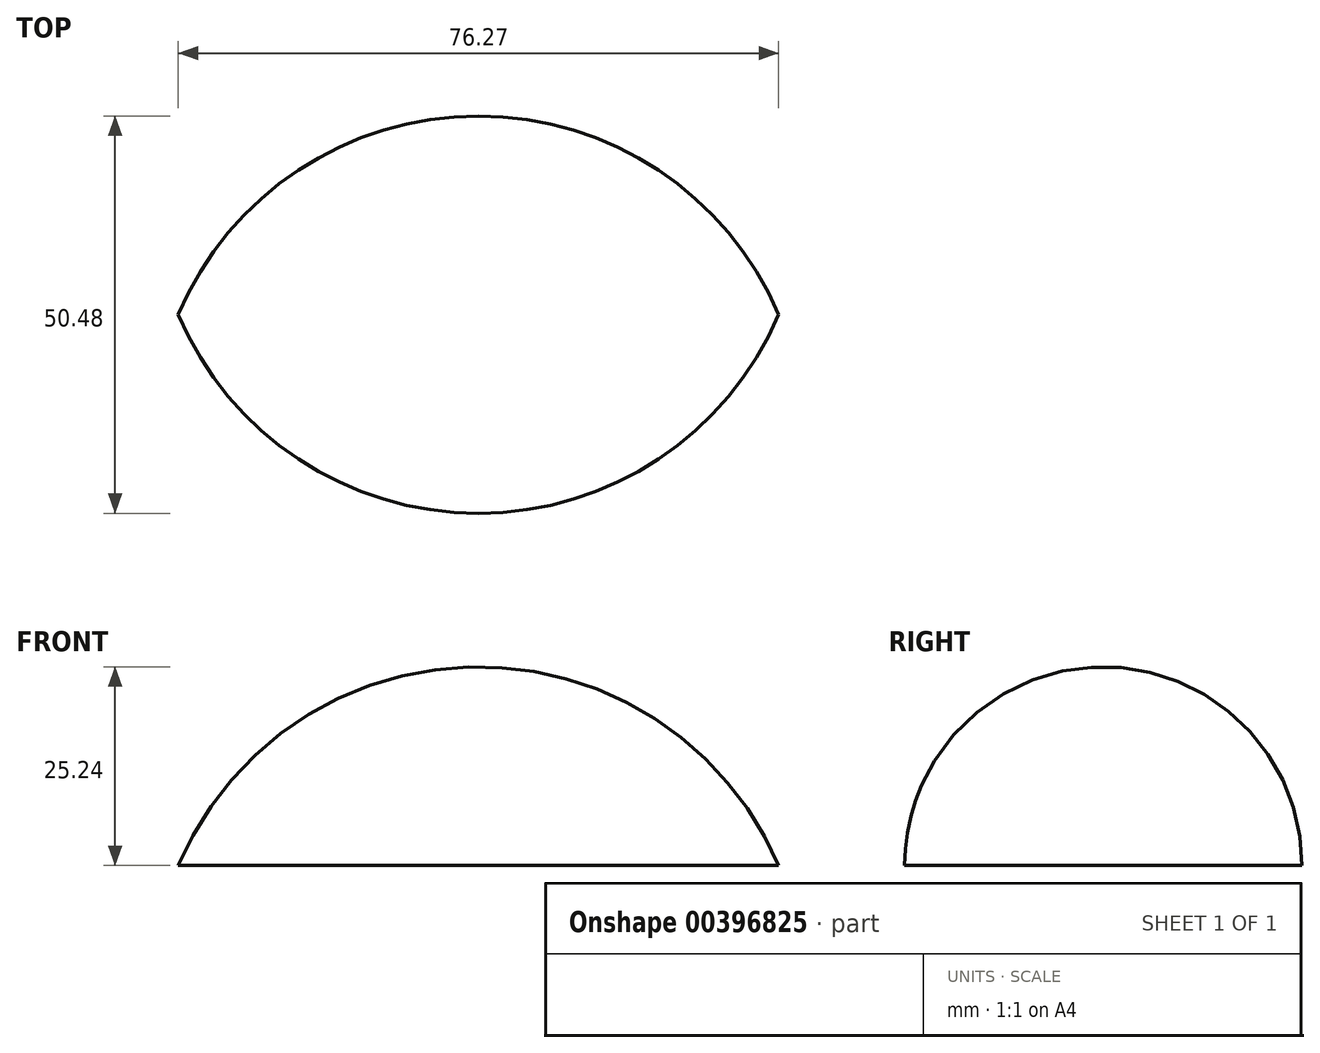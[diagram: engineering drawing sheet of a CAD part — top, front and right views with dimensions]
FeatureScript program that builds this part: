
annotation { "Feature Type Name" : "Feature", "Feature Type Description" : "" }
export const myFeature = defineFeature(function(context is Context, id is Id, definition is map)
    precondition{}
    {
        {
            var Q0;
            Q0=qCreatedBy(makeId("Front.planeOp"),FACE);
            var sketch = newSketch(context, id + "F0", { "sketchPlane" : qUnion([Q0])});
            skArc(sketch, "E0", {"start": v(41.73, 0) * mm, "mid": v(3.6, 25.24) * mm, "end": v(-34.54, 0) * mm});
            skLineSegment(sketch, "E1", {"start": v(-34.54, 0) * mm, "end": v(41.73, 0) * mm});
            skSolve(sketch);
        }
        {
            var Q0;
            Q0 = qSketchRegion(id + "F0", true);
            var Q1;
            Q1=sQuery(id+"F0.wireOp",EDGE,"E1");
            revolve(context, id + "F1", {"entities" : qUnion([Q0]), "axis" : qUnion([Q1]), "revolveType" : RevolveType.SYMMETRIC, "oppositeDirection" : true, "angle" : 180 * degree});
        }
    });
